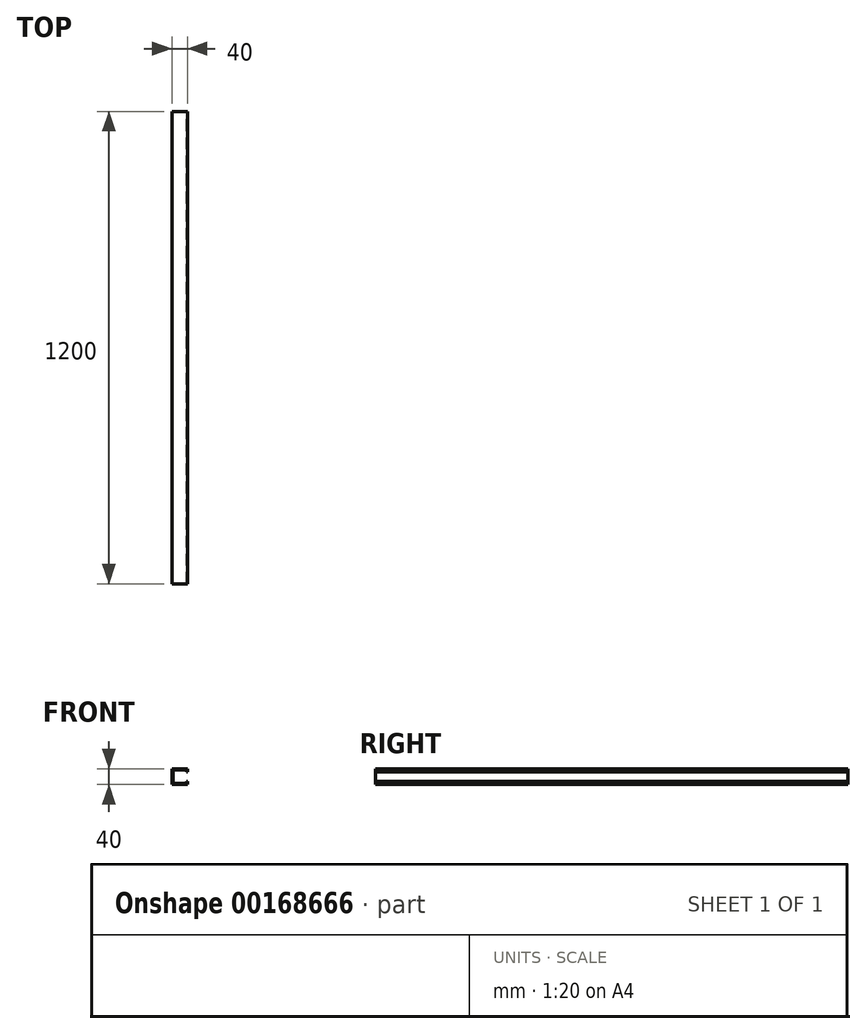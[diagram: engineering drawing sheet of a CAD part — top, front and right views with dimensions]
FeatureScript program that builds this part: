
annotation { "Feature Type Name" : "Feature", "Feature Type Description" : "" }
export const myFeature = defineFeature(function(context is Context, id is Id, definition is map)
    precondition{}
    {
        {
            var Q0;
            Q0=qCreatedBy(makeId("Front.planeOp"),FACE);
            var sketch = newSketch(context, id + "F0", { "sketchPlane" : qUnion([Q0])});
            skLineSegment(sketch, "E0.bottom", {"start": v(20, 20) * mm, "end": v(-20, 20) * mm});
            skLineSegment(sketch, "E0.top", {"start": v(20, -20) * mm, "end": v(-20, -20) * mm});
            skLineSegment(sketch, "E0.right", {"start": v(-20, 20) * mm, "end": v(-20, -20) * mm});
            skPoint(sketch, "E0.middle", {"position": v(0, 0) * mm});
            skLineSegment(sketch, "E1.0", {"start": v(17, -17) * mm, "end": v(-17, -17) * mm});
            skLineSegment(sketch, "E1.1", {"start": v(-17, 17) * mm, "end": v(-17, -17) * mm});
            skLineSegment(sketch, "E1.2", {"start": v(17, 17) * mm, "end": v(-17, 17) * mm});
            skLineSegment(sketch, "E2", {"start": v(17, 17) * mm, "end": v(17, 12) * mm});
            skLineSegment(sketch, "E3", {"start": v(17, 12) * mm, "end": v(20, 12) * mm});
            skLineSegment(sketch, "E4", {"start": v(20, -12) * mm, "end": v(17, -12) * mm});
            skLineSegment(sketch, "E5", {"start": v(17, -12) * mm, "end": v(17, -17) * mm});
            skLineSegment(sketch, "E6", {"start": v(20, 20) * mm, "end": v(20, 12) * mm});
            skLineSegment(sketch, "E7", {"start": v(20, -20) * mm, "end": v(20, -12) * mm});
            skSolve(sketch);
        }
        {
            var Q0;
            Q0=makeQuery(id+"F0.imprint","IMPRINT",FACE,{"disambiguationData":[TD([[makeQuery(id+"F0.imprint","IMPRINT",EDGE,{"derivedFrom":sQuery(id+"F0.wireOp",EDGE,"E0.bottom")}),1.0]])]});
            extrude(context, id + "F1", {"entities" : qUnion([Q0]), "depth" : 1200 * mm});
        }
    });
